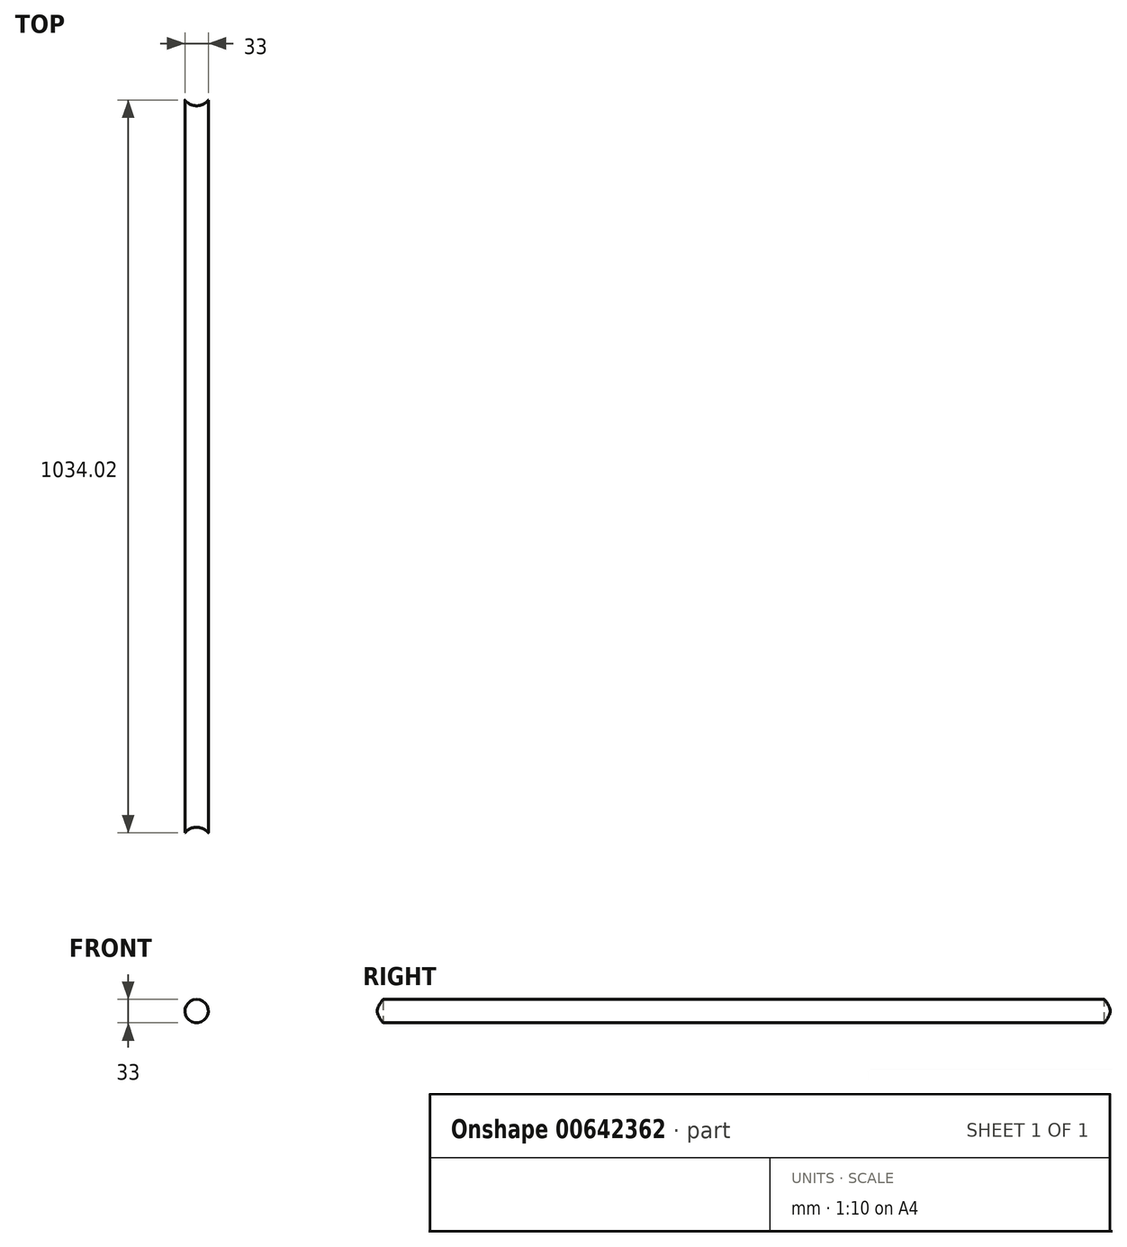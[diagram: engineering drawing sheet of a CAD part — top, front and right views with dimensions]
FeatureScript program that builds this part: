
annotation { "Feature Type Name" : "Feature", "Feature Type Description" : "" }
export const myFeature = defineFeature(function(context is Context, id is Id, definition is map)
    precondition{}
    {
        {
            var Q0;
            Q0=qCreatedBy(makeId("Front.planeOp"),FACE);
            var sketch = newSketch(context, id + "F0", { "sketchPlane" : qUnion([Q0])});
            skCircle(sketch, "E0", {"center": v(0, 0) * mm, "radius": 16.5 * mm});
            skSolve(sketch);
        }
        {
            var Q0;
            Q0=makeQuery(id+"F0.imprint","IMPRINT",FACE,{"disambiguationData":[TD([[makeQuery(id+"F0.imprint","IMPRINT",EDGE,{"derivedFrom":sQuery(id+"F0.wireOp",EDGE,"E0")}),1.0]])]});
            extrude(context, id + "F1", {"entities" : qUnion([Q0]), "depth" : 1060 * mm, "offsetDistance" : 25 * mm});
        }
        {
            var Q0;
            Q0=qCreatedBy(makeId("Top.planeOp"),FACE);
            var sketch = newSketch(context, id + "F2", { "sketchPlane" : qUnion([Q0])});
            skCircle(sketch, "E1", {"center": v(0, 0) * mm, "radius": 21 * mm});
            skSolve(sketch);
        }
        {
            var Q0;
            Q0=qSketchRegion(id+"F2",true);
            extrude(context, id + "F3", {"entities" : qUnion([Q0]), "operationType" : NewBodyOperationType.REMOVE, "endBound" : BoundingType.SYMMETRIC, "oppositeDirection" : true, "depth" : 1000 * mm, "offsetDistance" : 25 * mm});
        }
        {
            var Q0;
            Q0=qCreatedBy(makeId("Top.planeOp"),FACE);
            var sketch = newSketch(context, id + "F4", { "sketchPlane" : qUnion([Q0])});
            skLineSegment(sketch, "E2", {"start": v(0, -1060) * mm, "end": v(21, -1060) * mm});
            skLineSegment(sketch, "E3", {"start": v(0, -1060) * mm, "end": v(-21, -1060) * mm});
            skArc(sketch, "E4", {"start": v(21, -1060) * mm, "mid": v(0, -1039) * mm, "end": v(-21, -1060) * mm});
            skSolve(sketch);
        }
        {
            var Q0;
            Q0 = qSketchRegion(id + "F4", true);
            extrude(context, id + "F5", {"entities" : qUnion([Q0]), "operationType" : NewBodyOperationType.REMOVE, "endBound" : BoundingType.SYMMETRIC, "depth" : 100 * mm, "offsetDistance" : 25 * mm});
        }
    });
